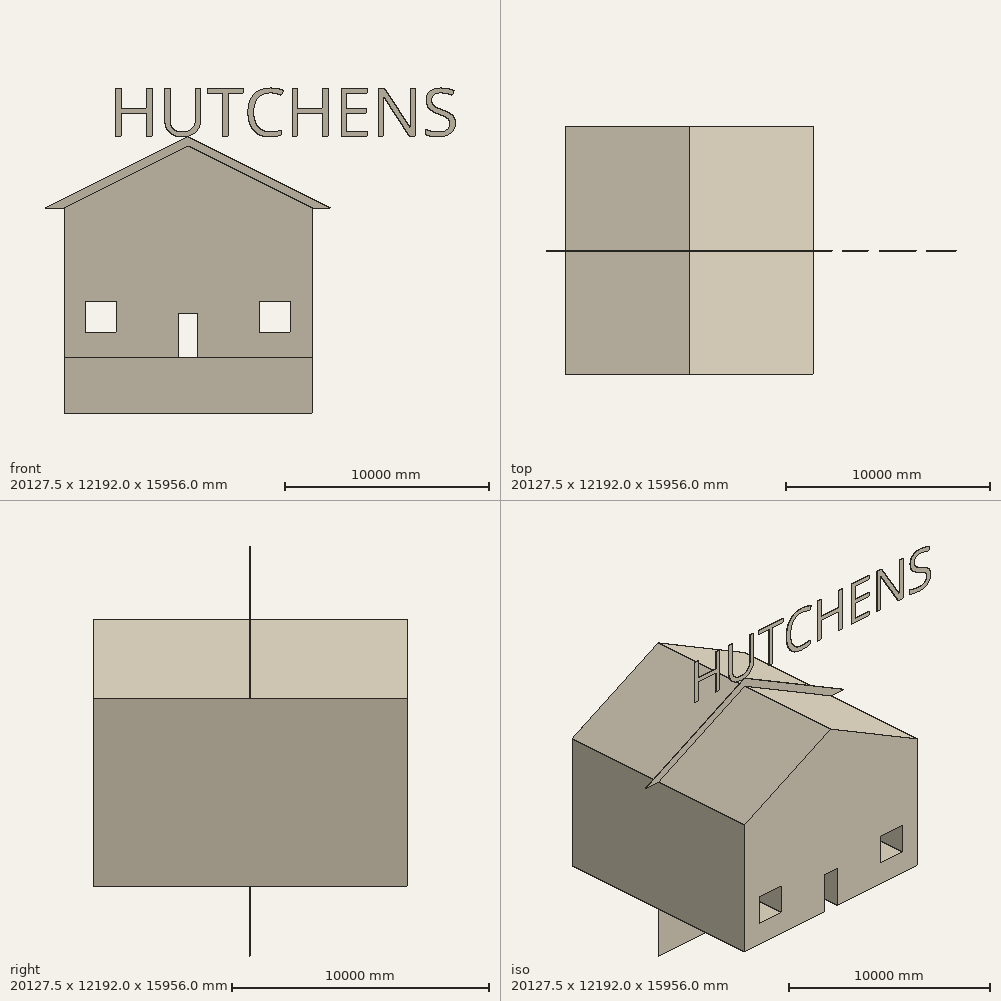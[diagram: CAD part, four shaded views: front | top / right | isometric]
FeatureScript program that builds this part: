
annotation { "Feature Type Name" : "Feature", "Feature Type Description" : "" }
export const myFeature = defineFeature(function(context is Context, id is Id, definition is map)
    precondition{}
    {
        {
            var Q0;
            Q0=qCreatedBy(makeId("Front.planeOp"),FACE);
            var sketch = newSketch(context, id + "F0", { "sketchPlane" : qUnion([Q0])});
            skLineSegment(sketch, "E0", {"start": v(0, 0) * mm, "end": v(-6096, 0) * mm});
            skLineSegment(sketch, "E1", {"start": v(0, 0) * mm, "end": v(6096, 0) * mm});
            skLineSegment(sketch, "E2", {"start": v(0, 0) * mm, "end": v(0, 3048) * mm});
            skLineSegment(sketch, "E3", {"start": v(-6096, 0) * mm, "end": v(0, 3048) * mm});
            skLineSegment(sketch, "E4", {"start": v(-6096, 0) * mm, "end": v(-7010.4, 0) * mm});
            skLineSegment(sketch, "E5", {"start": v(6096, 0) * mm, "end": v(7010.4, 0) * mm});
            skLineSegment(sketch, "E6", {"start": v(0, 3048) * mm, "end": v(0, 3505.2) * mm});
            skLineSegment(sketch, "E7", {"start": v(7010.4, 0) * mm, "end": v(0, 3505.2) * mm});
            skLineSegment(sketch, "E8", {"start": v(0, 3505.2) * mm, "end": v(-7010.4, 0) * mm});
            skLineSegment(sketch, "E9", {"start": v(-6096, 0) * mm, "end": v(-6096, -7315.2) * mm});
            skLineSegment(sketch, "E10", {"start": v(6096, 0) * mm, "end": v(6096, -7315.2) * mm});
            skLineSegment(sketch, "E11", {"start": v(6096, -7315.2) * mm, "end": v(-6096, -7315.2) * mm});
            skLineSegment(sketch, "E12", {"start": v(-6096, -7315.2) * mm, "end": v(-6096, -7620) * mm});
            skLineSegment(sketch, "E13", {"start": v(6096, -7315.2) * mm, "end": v(6096, -7620) * mm});
            skLineSegment(sketch, "E14", {"start": v(0, -7315.2) * mm, "end": v(-457.2, -7315.2) * mm});
            skLineSegment(sketch, "E15", {"start": v(0, -7315.2) * mm, "end": v(457.2, -7315.2) * mm});
            skLineSegment(sketch, "E16", {"start": v(-457.2, -7315.2) * mm, "end": v(-457.2, -5181.6) * mm});
            skLineSegment(sketch, "E17", {"start": v(457.2, -7315.2) * mm, "end": v(457.2, -5181.6) * mm});
            skLineSegment(sketch, "E18", {"start": v(-457.2, -5181.6) * mm, "end": v(457.2, -5181.6) * mm});
            skCircle(sketch, "E19", {"center": v(304.8, -6248.4) * mm, "radius": 116.01 * mm});
            skPoint(sketch, "E19.centerSnap0", {"position": v(457.2, -6248.4) * mm});
            skLineSegment(sketch, "E20", {"start": v(-5029.2, -4572) * mm, "end": v(-5029.2, -6096) * mm});
            skLineSegment(sketch, "E21", {"start": v(-5029.2, -6096) * mm, "end": v(-3505.2, -6096) * mm});
            skLineSegment(sketch, "E22", {"start": v(-3505.2, -6096) * mm, "end": v(-3505.2, -4572) * mm});
            skLineSegment(sketch, "E23", {"start": v(-3505.2, -4572) * mm, "end": v(-5029.2, -4572) * mm});
            skLineSegment(sketch, "E24", {"start": v(3505.2, -6096) * mm, "end": v(3505.2, -4572) * mm});
            skLineSegment(sketch, "E25", {"start": v(3505.2, -6096) * mm, "end": v(5029.2, -6096) * mm});
            skLineSegment(sketch, "E26", {"start": v(3505.2, -4572) * mm, "end": v(5029.2, -4572) * mm});
            skLineSegment(sketch, "E27", {"start": v(5029.2, -4572) * mm, "end": v(5029.2, -6096) * mm});
            skText(sketch, "E28", { "text": "HUTCHENS", "fontName": "OpenSans-Regular.ttf"});
            skLineSegment(sketch, "E29", {"start": v(-6096, -7620) * mm, "end": v(6096, -7620) * mm});
            skLineSegment(sketch, "E30", {"start": v(0, 3048) * mm, "end": v(6096, 0) * mm});
            skLineSegment(sketch, "E31", {"start": v(6096, -7620) * mm, "end": v(6096, -10058.4) * mm});
            skLineSegment(sketch, "E32", {"start": v(6096, -10058.4) * mm, "end": v(-6096, -10058.4) * mm});
            skLineSegment(sketch, "E33", {"start": v(-6096, -7620) * mm, "end": v(-6096, -10058.4) * mm});
            const initialGuessF0  = {"E28": [-3.87348, 3.53121, 1, 0, 2.3531]};
            skSetInitialGuess(sketch, initialGuessF0);
            skSolve(sketch);
        }
        {
            var Q0;
            Q0 = qSketchRegion(id + "F0", true);
            extrude(context, id + "F1", {"entities" : qUnion([Q0]), "depth" : 30.48 * mm, "offsetDistance" : 30.48 * mm});
        }
        {
            var Q0;
            Q0=makeQuery(id+"F0.imprint","IMPRINT",FACE,{"disambiguationData":[TD([[makeQuery(id+"F0.imprint","IMPRINT",EDGE,{"derivedFrom":sQuery(id+"F0.wireOp",EDGE,"E0")}),-1.0]])]});
            var Q1;
            Q1=makeQuery(id+"F0.imprint","IMPRINT",FACE,{"disambiguationData":[TD([[makeQuery(id+"F0.imprint","IMPRINT",EDGE,{"derivedFrom":sQuery(id+"F0.wireOp",EDGE,"E1")}),1.0]])]});
            var Q2;
            Q2=makeQuery(id+"F0.imprint","IMPRINT",FACE,{"disambiguationData":[TD([[makeQuery(id+"F0.imprint","IMPRINT",EDGE,{"derivedFrom":sQuery(id+"F0.wireOp",EDGE,"E0")}),1.0]])]});
            extrude(context, id + "F2", {"entities" : qUnion([Q0, Q1, Q2]), "operationType" : NewBodyOperationType.ADD, "endBound" : BoundingType.SYMMETRIC, "depth" : 12192 * mm, "offsetDistance" : 30.48 * mm});
        }
    });
